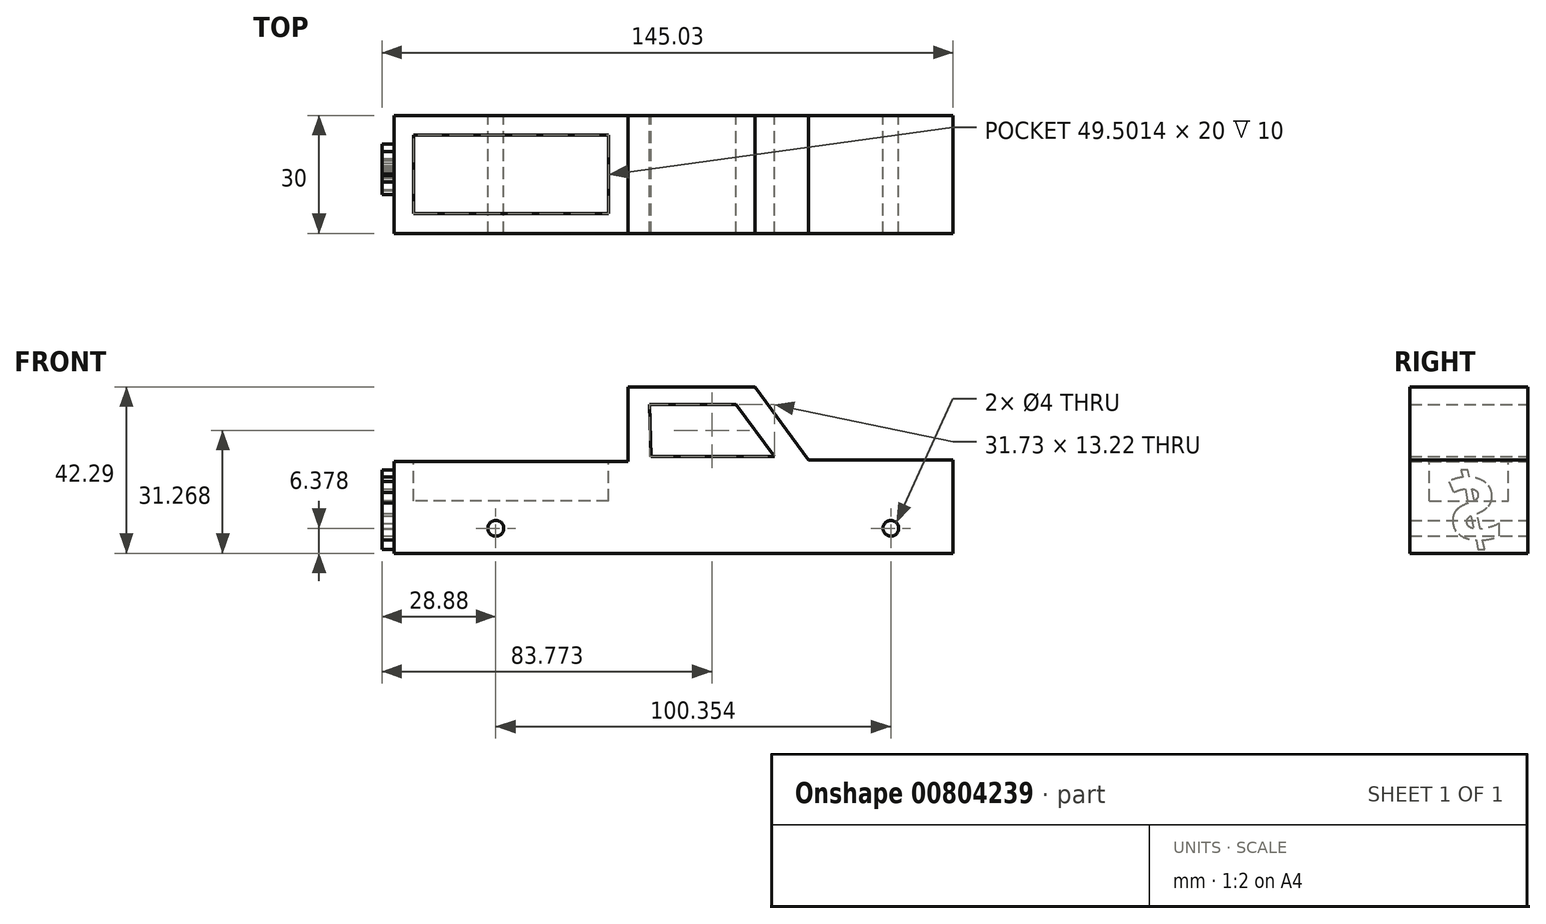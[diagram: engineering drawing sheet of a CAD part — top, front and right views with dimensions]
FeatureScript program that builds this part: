
annotation { "Feature Type Name" : "Feature", "Feature Type Description" : "" }
export const myFeature = defineFeature(function(context is Context, id is Id, definition is map)
    precondition{}
    {
        {
            var Q0;
            Q0=qCreatedBy(makeId("Front.planeOp"),FACE);
            var sketch = newSketch(context, id + "F0", { "sketchPlane" : qUnion([Q0])});
            skLineSegment(sketch, "E0", {"start": v(-914.56, -118.36) * mm, "end": v(-772.53, -118.36) * mm});
            skLineSegment(sketch, "E1", {"start": v(-772.53, -118.36) * mm, "end": v(-772.53, -94.58) * mm});
            skLineSegment(sketch, "E2", {"start": v(-772.53, -94.58) * mm, "end": v(-809.22, -94.58) * mm});
            skLineSegment(sketch, "E3", {"start": v(-809.22, -94.58) * mm, "end": v(-822.88, -76.07) * mm});
            skLineSegment(sketch, "E4", {"start": v(-822.88, -76.07) * mm, "end": v(-855.06, -76.07) * mm});
            skLineSegment(sketch, "E5", {"start": v(-855.06, -76.07) * mm, "end": v(-855.06, -95.02) * mm});
            skLineSegment(sketch, "E6", {"start": v(-855.06, -95.02) * mm, "end": v(-914.56, -95.02) * mm});
            skLineSegment(sketch, "E7", {"start": v(-914.56, -95.02) * mm, "end": v(-914.56, -118.36) * mm});
            skLineSegment(sketch, "E8", {"start": v(-849.65, -80.48) * mm, "end": v(-827.62, -80.48) * mm});
            skLineSegment(sketch, "E9", {"start": v(-827.62, -80.48) * mm, "end": v(-817.92, -93.7) * mm});
            skLineSegment(sketch, "E10", {"start": v(-817.92, -93.7) * mm, "end": v(-849.21, -93.7) * mm});
            skLineSegment(sketch, "E11", {"start": v(-849.21, -93.7) * mm, "end": v(-849.65, -80.48) * mm});
            skCircle(sketch, "E12", {"center": v(-888.68, -111.98) * mm, "radius": 2 * mm});
            skCircle(sketch, "E13", {"center": v(-788.33, -111.98) * mm, "radius": 2 * mm});
            skSolve(sketch);
        }
        {
            var Q0;
            Q0 = qSketchRegion(id + "F0", true);
            extrude(context, id + "F1", {"entities" : qUnion([Q0]), "depth" : 30 * mm, "offsetDistance" : 25 * mm});
        }
        {
            var Q0;
            Q0=makeQuery(id+"F1.opExtrude","SWEPT_FACE",FACE,{"disambiguationData":[OSD([sQuery(id+"F0.wireOp",EDGE,"E7")])]});
            var sketch = newSketch(context, id + "F2", { "sketchPlane" : qUnion([Q0])});
            skText(sketch, "E14", { "text": "$", "fontName": "OpenSans-BoldItalic.ttf"});
            const initialGuessF2  = {"E14": [0.00665, -0.11595, 1, 0, 0.01779]};
            skSetInitialGuess(sketch, initialGuessF2);
            skSolve(sketch);
        }
        {
            var Q0;
            Q0=makeQuery(id+"F2.imprint","IMPRINT",FACE,{"disambiguationData":[TD([[makeQuery(id+"F2.imprint","IMPRINT",EDGE,{"derivedFrom":sQuery(id+"F2.wireOp",EDGE,"E14.sketch_text.stroke-0")}),-1.0]])]});
            extrude(context, id + "F3", {"entities" : qUnion([Q0]), "operationType" : NewBodyOperationType.ADD, "depth" : 3 * mm, "offsetDistance" : 25 * mm});
        }
        {
            var Q0;
            Q0=makeQuery(id+"F1.opExtrude","SWEPT_FACE",FACE,{"disambiguationData":[OSD([sQuery(id+"F0.wireOp",EDGE,"E6")])]});
            var sketch = newSketch(context, id + "F4", { "sketchPlane" : qUnion([Q0])});
            skLineSegment(sketch, "E15.0", {"start": v(-860.06, -5) * mm, "end": v(-909.56, -5) * mm});
            skLineSegment(sketch, "E15.1", {"start": v(-860.06, -25) * mm, "end": v(-860.06, -5) * mm});
            skLineSegment(sketch, "E15.2", {"start": v(-860.06, -25) * mm, "end": v(-909.56, -25) * mm});
            skLineSegment(sketch, "E15.3", {"start": v(-909.56, -25) * mm, "end": v(-909.56, -5) * mm});
            skSolve(sketch);
        }
        {
            var Q0;
            Q0 = qSketchRegion(id + "F4", true);
            extrude(context, id + "F5", {"entities" : qUnion([Q0]), "operationType" : NewBodyOperationType.REMOVE, "oppositeDirection" : true, "depth" : 10 * mm, "offsetDistance" : 25 * mm});
        }
    });
